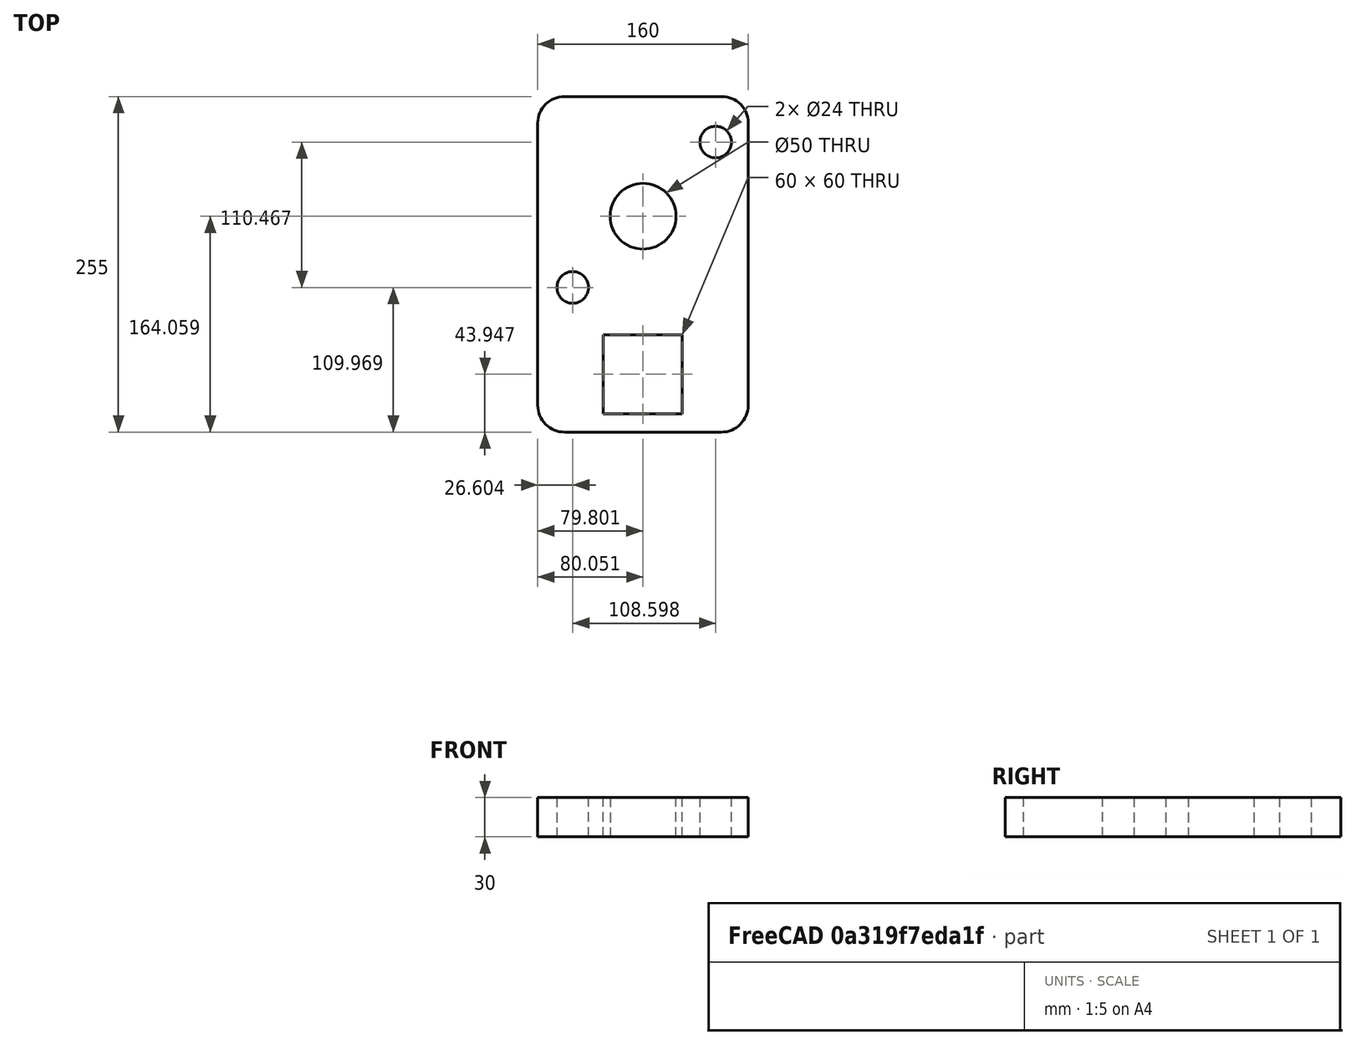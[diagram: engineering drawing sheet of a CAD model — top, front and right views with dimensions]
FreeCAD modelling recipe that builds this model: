
FCSTD DOCUMENT  (FreeCAD 0.18R16131 (Git))
Label: Momentum_Main(2)_Plate_1-1_160X200_12T_25mm(lm12uu)
License: All rights reserved
LicenseURL: http://en.wikipedia.org/wiki/All_rights_reserved
objects: PartDesign::Pad×2, Sketcher::SketchObject×1, PartDesign::Body×1
note: 6 computed .brp shape members not serialized (recipe doc carries the construction recipe); baked Part::Feature solids carry a one-line shape summary decoded from their .brp

FEATURE [Sketcher::SketchObject] Sketch
  MapMode = 5
  Support = -> [XY_Plane]
  sketch-geometry (15):
    g0: Circle CenterX=0.120778 CenterY=29.9192 CenterZ=0 NormalX=0 NormalY=0 NormalZ=1 AngleXU=0 Radius=25
    g1: Circle CenterX=-53.3259 CenterY=-24.1714 CenterZ=0 NormalX=0 NormalY=0 NormalZ=1 AngleXU=0 Radius=12
    g2: Circle CenterX=55.2719 CenterY=86.2952 CenterZ=0 NormalX=0 NormalY=0 NormalZ=1 AngleXU=0 Radius=12
    g3: LineSegment StartX=-30.1291 StartY=-120.193 StartZ=0 EndX=29.8709 EndY=-120.193 EndZ=0
    g4: LineSegment StartX=29.8709 StartY=-120.193 StartZ=0 EndX=29.8709 EndY=-60.1926 EndZ=0
    g5: LineSegment StartX=29.8709 StartY=-60.1926 StartZ=0 EndX=-30.1291 EndY=-60.1926 EndZ=0
    g6: LineSegment StartX=-30.1291 StartY=-60.1926 StartZ=0 EndX=-30.1291 EndY=-120.193 EndZ=0
    g7: LineSegment StartX=-59.3423 StartY=-134.144 StartZ=0 EndX=59.5153 EndY=-134.144 EndZ=0
    g8: LineSegment StartX=80.0668 StartY=-113.592 StartZ=0 EndX=80.0668 EndY=100.872 EndZ=0
    g9: LineSegment StartX=60.0827 StartY=120.856 StartZ=0 EndX=-59.6894 EndY=120.856 EndZ=0
    g10: LineSegment StartX=-79.9332 StartY=100.613 StartZ=0 EndX=-79.9332 EndY=-113.553 EndZ=0
    g11: ArcOfCircle CenterX=60.0827 CenterY=100.872 CenterZ=0 NormalX=0 NormalY=0 NormalZ=1 AngleXU=0 Radius=19.9841 StartAngle=0 EndAngle=1.5708
    g12: ArcOfCircle CenterX=-59.6894 CenterY=100.613 CenterZ=0 NormalX=0 NormalY=0 NormalZ=1 AngleXU=0 Radius=20.2438 StartAngle=1.5708 EndAngle=3.14159
    g13: ArcOfCircle CenterX=59.5153 CenterY=-113.592 CenterZ=0 NormalX=0 NormalY=0 NormalZ=1 AngleXU=0 Radius=20.5515 StartAngle=4.71239 EndAngle=6.28319
    g14: ArcOfCircle CenterX=-59.3423 CenterY=-113.553 CenterZ=0 NormalX=0 NormalY=0 NormalZ=1 AngleXU=0 Radius=20.5909 StartAngle=3.14159 EndAngle=4.71239
  constraints (25):
    c: Radius(g0) = 25
    c: Radius(g1) = 12
    c: Radius(g2) = 12
    c: Coincident(g3,g4)
    c: Coincident(g4,g5)
    c: Coincident(g5,g6)
    c: Coincident(g6,g3)
    c: Horizontal(g3)
    c: Horizontal(g5)
    c: Vertical(g4)
    c: Vertical(g6)
    c: DistanceX(g5,g5) = 60
    c: DistanceY(g4,g4) = 60
    c: Horizontal(g7)
    c: Horizontal(g9)
    c: Vertical(g8)
    c: Vertical(g10)
    c: Tangent(g9,g11) = -1.5708
    c: Tangent(g8,g11) = -1.5708
    c: Tangent(g9,g12) = -1.5708
    c: Tangent(g10,g12) = -1.5708
    c: Tangent(g8,g13) = -1.5708
    c: Tangent(g7,g13) = -1.5708
    c: Tangent(g7,g14) = -1.5708
    c: Tangent(g10,g14) = -1.5708
FEATURE [PartDesign::Pad] Pad
  Length = 30
  Length2 = 100
  Profile = -> Sketch
  Type = 0
FEATURE [PartDesign::Pad] Pad001
  BaseFeature = -> Pad
  Length = 30
  Length2 = 100
  Profile = -> Sketch
  Type = 0
FEATURE [PartDesign::Body] Body
  Group = -> [Sketch,Pad,Pad001]
  Origin = -> Origin
  Tip = -> Pad001
